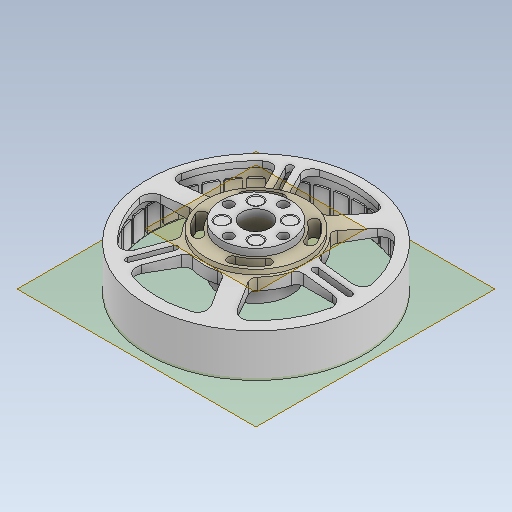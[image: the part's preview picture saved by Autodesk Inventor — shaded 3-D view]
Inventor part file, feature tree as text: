
AUTODESK INVENTOR PART (.ipt)
format: ipt  version: 2020 (Build 240168000, 168)  size: 1,058,304 bytes
history: native  units: mm
features: sketch x12, extrude x11, projected_geometry x9, pattern_circular x6, fillet x5, plane x2, revolve x1, thicken_offset x1
ambient origin geometry x8: Origin, YZ Plane, XZ Plane, XY Plane, X Axis, Y Axis, Z Axis, Center Point
bodies: Solid1 (feature_tree)
feature tree (47):
  extrude  "Extrusion1"  Depth=2.5mm
  extrude  "Extrusion2"  Depth=7.0mm TaperAngle=0.0deg
  revolve  "Revolution1"  [1 undecoded]
  plane  "Work Plane1"
  extrude  "Extrusion3"  Depth=10.0mm
  fillet  "Fillet1"  [1 undecoded]
  fillet  "Fillet2"  [1 undecoded]
  pattern_circular  "Circular Pattern1"  Count=6 Angle=360.0deg
  extrude  "Extrusion4"  Depth=4.0mm
  pattern_circular  "Circular Pattern2"  Count=6 Angle=360.0deg
  extrude  "Extrusion5"  Depth=7.0mm
  extrude  "Extrusion6"  Depth=0.5mm TaperAngle=0.0deg
  pattern_circular  "Circular Pattern3"  Count=3 Angle=360.0deg
  extrude  "Extrusion7"  Depth=0.5mm
  extrude  "Extrusion8"  Depth=0.5mm TaperAngle=0.0deg
  extrude  "Extrusion9"  Depth=0.5mm
  fillet  "Fillet3"  Radius=4.0mm
  pattern_circular  "Circular Pattern4"  Count=2  [1 undecoded]
  extrude  "Extrusion10"  Depth=0.5mm TaperAngle=360.0deg
  pattern_circular  "Circular Pattern5"  [2 undecoded]
  fillet  "Fillet4"  Radius=20.0mm
  thicken_offset  "Thicken1"
  plane  "Work Plane2"
  extrude  "Extrusion11"  Depth=10.0mm TaperAngle=0.0deg
  fillet  "Fillet5"  Radius=39.0mm
  pattern_circular  "Circular Pattern6"  [2 undecoded]
  sketch  "Sketch1"  dims[d0=91.0mm d1=2.5mm]
  sketch  "Sketch2"  dims[d2=23.0mm d3=0.0mm d4=7.0mm d5=0.0mm]
  sketch  "Sketch3"  dims[d6=21.0mm d7=2.0mm]
  projected_geometry  "Projected Loop1"
  sketch  "Sketch4"  dims[d8=18.0mm d9=10.0mm d10=90.0deg d11=0.0mm]
  projected_geometry  "Projected Loop2"
  sketch  "Sketch5"  dims[d12=44.0mm]
  projected_geometry  "Projected Loop3"
  sketch  "Sketch6"  dims[d13=82.0mm]
  projected_geometry  "Projected Loop4"
  sketch  "Sketch7"  dims[d14=8.0mm]
  projected_geometry  "Projected Loop5"
  sketch  "Sketch8"  dims[d15=22.0mm d16=60.0mm d18=360.0deg]
  sketch  "Sketch9"  dims[d20=7.0mm d21=0.0mm d22=4.0mm]
  projected_geometry  "Projected Loop6"
  sketch  "Sketch10"  dims[d23=3.0mm d24=60.0mm d25=360.0deg]
  projected_geometry  "Projected Loop7"
  sketch  "Sketch11"  dims[d27=22.0mm d28=7.0mm]
  projected_geometry  "Projected Loop8"
  sketch  "Sketch12"  dims[d29=2.5mm d30=7.0mm d31=0.0mm d32=30.0mm d33=360.0deg d35=29.0mm d36=3.0mm d37=0.0mm d38=11.45mm d39=4.0mm d40=20.0mm d41=0.0mm d42=40.0mm d43=360.0deg d45=11.8mm d46=20.0mm d47=0.0mm d48=10.0mm d49=0.0mm d50=39.0mm d51=31.0mm d52=15.0deg d53=4.886922mm d54=10.0mm d55=0.0mm d56=2.0mm d57=40.0mm d58=360.0deg d60=2.0mm d61=6.0mm d62=0.2mm d63=0.0mm d64=40.0mm d65=360.0deg d67=0.5mm d68=0.5mm d69=0.5mm d70=-1.0mm d71=0.7mm d72=5.5mm d73=3.0mm d74=10.0mm d75=0.0mm d76=0.5mm d77=400.0mm d78=360.0deg]
  projected_geometry  "Projected Loop9"
note: 8 required parameter values undecoded (feature->parameter linkage not recoverable at this tier; creation-order binding heuristic only, values carry confidence <= 0.55)